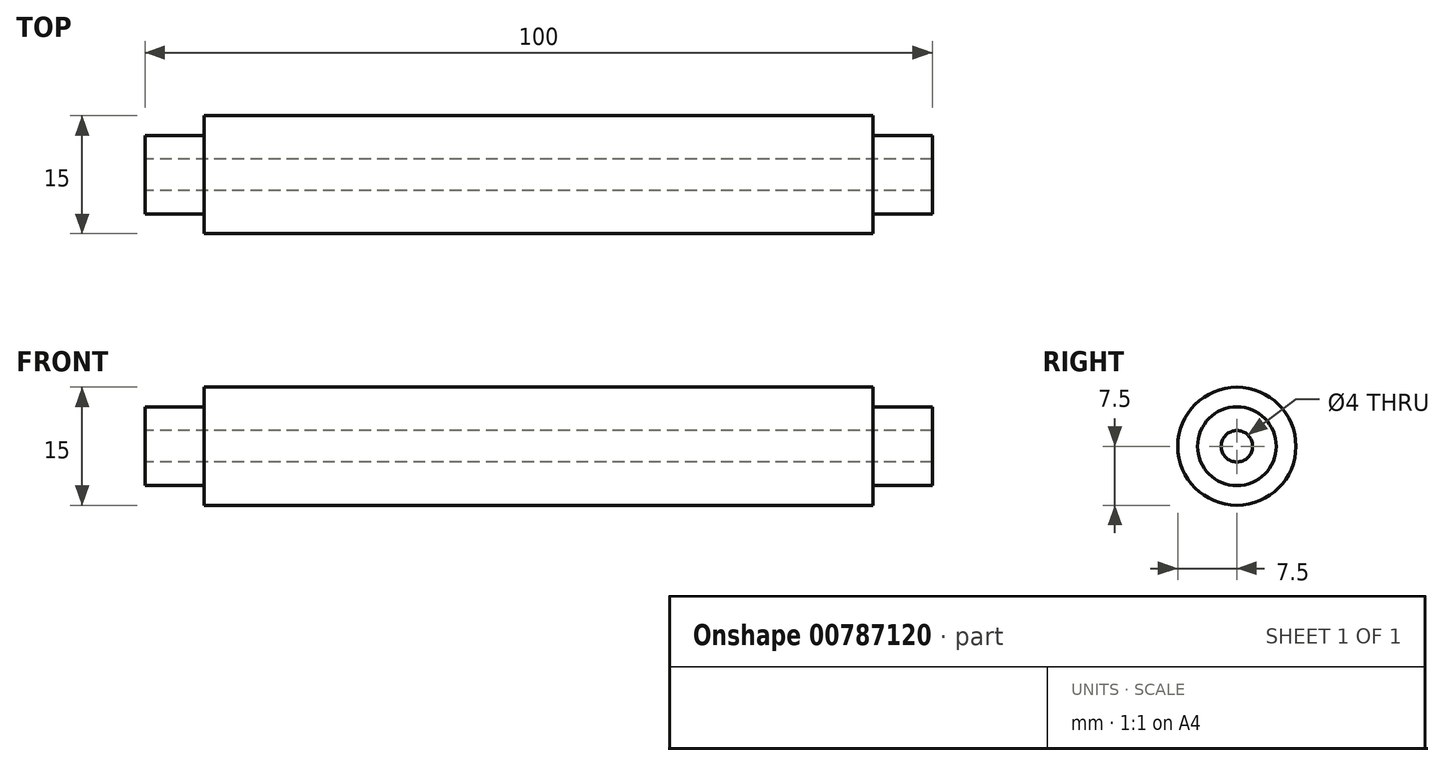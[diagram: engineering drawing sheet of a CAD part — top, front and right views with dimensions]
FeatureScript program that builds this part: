
annotation { "Feature Type Name" : "Feature", "Feature Type Description" : "" }
export const myFeature = defineFeature(function(context is Context, id is Id, definition is map)
    precondition{}
    {
        {
            var Q0;
            Q0=qCreatedBy(makeId("Front.planeOp"),FACE);
            var sketch = newSketch(context, id + "F0", { "sketchPlane" : qUnion([Q0])});
            skLineSegment(sketch, "E0.bottom", {"start": v(-42.5, -7.5) * mm, "end": v(42.5, -7.5) * mm});
            skLineSegment(sketch, "E0.top", {"start": v(-42.5, 7.5) * mm, "end": v(42.5, 7.5) * mm});
            skLineSegment(sketch, "E0.left", {"start": v(-42.5, -7.5) * mm, "end": v(-42.5, 7.5) * mm});
            skLineSegment(sketch, "E0.right", {"start": v(42.5, -7.5) * mm, "end": v(42.5, 7.5) * mm});
            skPoint(sketch, "E0.middle", {"position": v(0, 0) * mm});
            skLineSegment(sketch, "E1.left", {"start": v(-50, -5) * mm, "end": v(-50, 5) * mm});
            skLineSegment(sketch, "E1.right", {"start": v(50, -5) * mm, "end": v(50, 5) * mm});
            skLineSegment(sketch, "E2", {"start": v(-50, 0) * mm, "end": v(50, 0) * mm});
            skLineSegment(sketch, "E3", {"start": v(-50, 5) * mm, "end": v(-42.5, 5) * mm});
            skLineSegment(sketch, "E4", {"start": v(-50, -5) * mm, "end": v(-42.5, -5) * mm});
            skLineSegment(sketch, "E5", {"start": v(50, 5) * mm, "end": v(42.5, 5) * mm});
            skLineSegment(sketch, "E6", {"start": v(50, -5) * mm, "end": v(42.5, -5) * mm});
            skSolve(sketch);
        }
        {
            var Q0;
            {var subQ0=sQuery(id+"F0.wireOp",EDGE,"E4");Q0=makeQuery(id+"F0.imprint","IMPRINT",FACE,{"disambiguationData":[TD([[makeQuery(id+"F0.imprint","IMPRINT",EDGE,{"derivedFrom":subQ0}),1.0]])]});}
            var Q1;
            {var subQ1=sQuery(id+"F0.wireOp",EDGE,"E0.bottom");Q1=makeQuery(id+"F0.imprint","IMPRINT",FACE,{"disambiguationData":[TD([[makeQuery(id+"F0.imprint","IMPRINT",EDGE,{"derivedFrom":subQ1}),1.0]])]});}
            var Q2;
            {var subQ0=sQuery(id+"F0.wireOp",EDGE,"E6");Q2=makeQuery(id+"F0.imprint","IMPRINT",FACE,{"disambiguationData":[TD([[makeQuery(id+"F0.imprint","IMPRINT",EDGE,{"derivedFrom":subQ0}),-1.0]])]});}
            var Q3;
            Q3=sQuery(id+"F0.wireOp",EDGE,"E2");
            revolve(context, id + "F1", {"surfaceOperationType" : NewSurfaceOperationType.NEW, "entities" : qUnion([Q0, Q1, Q2]), "axis" : qUnion([Q3]), "revolveType" : RevolveType.FULL});
        }
        {
            var Q0;
            Q0=makeQuery(id+"F1.opRevolve","SWEPT_FACE",FACE,{"disambiguationData":[OSD([sQuery(id+"F0.wireOp",EDGE,"E1.left")])]});
            var sketch = newSketch(context, id + "F2", { "sketchPlane" : qUnion([Q0])});
            skPoint(sketch, "E7", {"position": v(0, 0) * mm});
            skSolve(sketch);
        }
        {
            var Q0;
            Q0=sQuery(id+"F2.wireOp",VERTEX,"E7");
            var Q1;
            Q1=makeQuery(id+"F1.opRevolve","SWEPT_BODY",BODY,{"disambiguationData":[OSD([sQuery(id+"F0.wireOp",EDGE,"E0.bottom"),sQuery(id+"F0.wireOp",EDGE,"E0.left"),sQuery(id+"F0.wireOp",EDGE,"E0.right"),sQuery(id+"F0.wireOp",EDGE,"E1.left"),sQuery(id+"F0.wireOp",EDGE,"E1.right"),sQuery(id+"F0.wireOp",EDGE,"E2"),sQuery(id+"F0.wireOp",EDGE,"E4"),sQuery(id+"F0.wireOp",EDGE,"E6")])]});
            hole(context, id + "F3", {"style" : HoleStyle.SIMPLE, "endStyle" : HoleEndStyle.THROUGH, "holeDiameter" : 4 * mm, "majorDiameter" : 5 * mm, "isTappedThrough" : true, "tappedDepth" : 12 * mm, "tapClearance" : 3, "locations" : qUnion([Q0]), "scope" : qUnion([Q1])});
        }
    });
